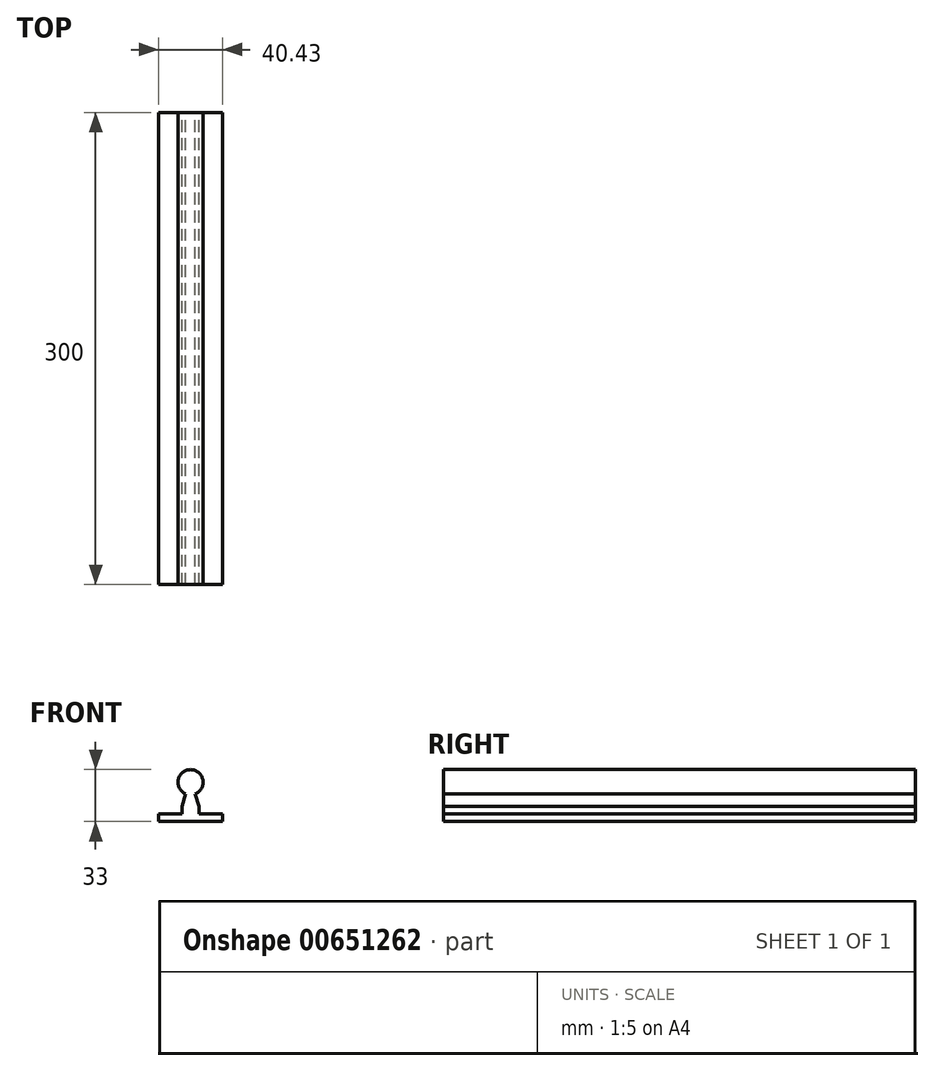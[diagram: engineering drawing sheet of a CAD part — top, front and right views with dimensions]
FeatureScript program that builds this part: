
annotation { "Feature Type Name" : "Feature", "Feature Type Description" : "" }
export const myFeature = defineFeature(function(context is Context, id is Id, definition is map)
    precondition{}
    {
        {
            var Q0;
            Q0=qCreatedBy(makeId("Front.planeOp"),FACE);
            var sketch = newSketch(context, id + "F0", { "sketchPlane" : qUnion([Q0])});
            skArc(sketch, "E0", {"start": v(3.03, -7.4) * mm, "mid": v(0, 8) * mm, "end": v(-3.03, -7.4) * mm});
            skLineSegment(sketch, "E1", {"start": v(0, -25) * mm, "end": v(-20.2, -25) * mm});
            skLineSegment(sketch, "E2", {"start": v(0, -25) * mm, "end": v(20.22, -25) * mm});
            skLineSegment(sketch, "E3", {"start": v(-20.2, -25) * mm, "end": v(-20.2, -20) * mm});
            skLineSegment(sketch, "E4", {"start": v(20.22, -25) * mm, "end": v(20.22, -20) * mm});
            skLineSegment(sketch, "E5", {"start": v(-3.03, -7.4) * mm, "end": v(-5.4, -15.42) * mm});
            skLineSegment(sketch, "E6", {"start": v(-5.4, -15.42) * mm, "end": v(-5.4, -20.15) * mm});
            skLineSegment(sketch, "E7", {"start": v(-5.4, -20.15) * mm, "end": v(-20.2, -20) * mm});
            skLineSegment(sketch, "E8.MirrorCS", {"start": v(3.03, -7.4) * mm, "end": v(5.4, -15.42) * mm});
            skLineSegment(sketch, "E9.MirrorCS", {"start": v(5.4, -15.42) * mm, "end": v(5.4, -20.15) * mm});
            skLineSegment(sketch, "E10.MirrorCS", {"start": v(5.4, -20.15) * mm, "end": v(20.22, -20) * mm});
            skSolve(sketch);
        }
        {
            var Q0;
            Q0=makeQuery(id+"F0.imprint","IMPRINT",FACE,{"disambiguationData":[TD([[makeQuery(id+"F0.imprint","IMPRINT",EDGE,{"derivedFrom":sQuery(id+"F0.wireOp",EDGE,"E0")}),1.0]])]});
            extrude(context, id + "F1", {"entities" : qUnion([Q0]), "depth" : 300 * mm, "offsetDistance" : 25.4 * mm});
        }
    });
